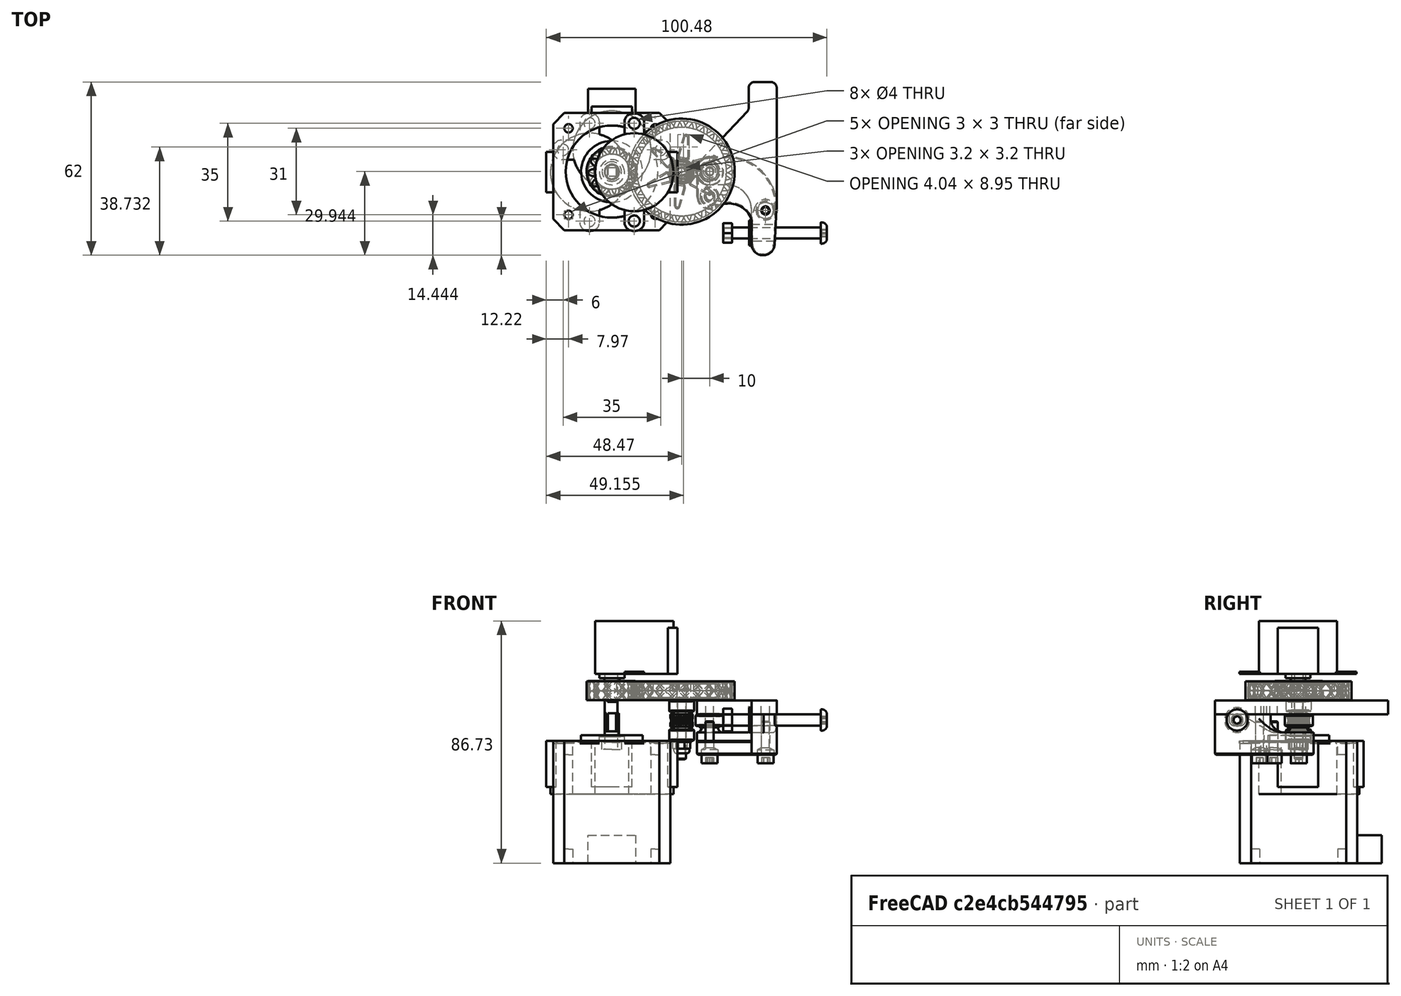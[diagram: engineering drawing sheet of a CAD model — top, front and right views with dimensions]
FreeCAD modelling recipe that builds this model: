
FCSTD DOCUMENT  (FreeCAD 0.16R6703 (Git))
Label: extruder-drive
License: All rights reserved
LicenseURL: http://en.wikipedia.org/wiki/All_rights_reserved
objects: Part::Cylinder×28, Part::Cut×24, Part::Feature×22, Part::MultiFuse×22, Part::Box×21, Part::Fillet×17, Part::Chamfer×5, Part::Mirroring×2, App::DocumentObjectGroup×1
note: 141 computed .brp shape members not serialized (recipe doc carries the construction recipe); baked Part::Feature solids carry a one-line shape summary decoded from their .brp

FEATURE [Part::Feature] Part__Feature  label="408-nema17-stepper"
  Placement = pos=(-0.129787,7.22389,-17.7265) rot=(0,0,-1;1.5708rad)
  shape: bbox 42 x 50.7 x 67.75 mm, 52 faces (baked)
FEATURE [Part::Feature] Part__Feature001  label="279"
  Placement = pos=(33.8857,6.14795,32.8235) rot=(0.910043,0.414513,0;3.14159rad)
  shape: bbox 10 x 10 x 4 mm, 22 faces (baked)
FEATURE [Part::Feature] Part__Feature002  label="1308_lasercut"
  Placement = pos=(34.8702,7.27962,40.5235) rot=(1,0,0;3.14159rad)
  shape: bbox 28.5 x 62 x 5 mm, 26 faces (baked)
FEATURE [Part::Feature] Part__Feature003  label="1309"
  Placement = pos=(34.8702,7.27962,29.0235) rot=(1,0,0;3.14159rad)
  shape: bbox 39.69 x 36.58 x 16.55 mm, 81 faces (baked)
FEATURE [Part::Feature] Part__Feature004  label="1193"
  Placement = pos=(39.681,-14.7761,33.5235) rot=(0.447214,0.774597,0.447214;1.82348rad)
  shape: bbox 3.2 x 7 x 8.083 mm, 26 faces (baked)
FEATURE [Part::Feature] Part__Feature005  label="650"
  Placement = pos=(74.681,-14.7761,33.5235) rot=(-0.322847,0.889685,-0.322847;1.68742rad)
  shape: bbox 37.2 x 8.193 x 8.193 mm, 18 faces (baked)
FEATURE [Part::Feature] Part__Feature006  label="1185"
  Placement = pos=(49.0702,-14.7761,33.5235) rot=(0.682107,-0.263555,0.682107;3.65698rad)
  shape: bbox 0.8 x 9 x 9 mm, 6 faces (baked)
FEATURE [Part::Feature] Part__Feature007  label="212"
  Placement = pos=(34.8702,7.27962,35.8235) rot=(0.929679,0.36837,0;3.14159rad)
  shape: bbox 7 x 7 x 0.5 mm, 6 faces (baked)
FEATURE [Part::Feature] Part__Feature008  label="257"
  Placement = pos=(34.8702,7.27962,21.0235) rot=(0.969952,-0.243295,0;3.14159rad)
  shape: bbox 5.7 x 5.7 x 15 mm, 16 faces (baked)
FEATURE [Part::Feature] Part__Feature010  label="212001"
  Placement = pos=(24.8702,7.22389,26.1235) rot=(0.905883,0.423527,0;3.14159rad)
  shape: bbox 7 x 7 x 0.5 mm, 6 faces (baked)
FEATURE [Part::Feature] Part__Feature011  label="212002"
  Placement = pos=(34.8702,7.27962,31.3235) rot=(0.929679,0.36837,0;3.14159rad)
  shape: bbox 7 x 7 x 0.5 mm, 6 faces (baked)
FEATURE [Part::Feature] Part__Feature012  label="448"
  Placement = pos=(24.8702,7.22389,30.1235) rot=(0,0,1;0rad)
  shape: bbox 8.761 x 8.744 x 6.4 mm, 204 faces (baked)
FEATURE [Part::Feature] Part__Feature013  label="423"
  Placement = pos=(24.8702,7.22389,39.0235) rot=(0,0,1;0.10732rad)
  shape: bbox 9 x 9 x 4 mm, 22 faces (baked)
FEATURE [Part::Feature] Part__Feature014  label="423001"
  Placement = pos=(24.8702,7.22389,28.6235) rot=(0,0,1;3.74342rad)
  shape: bbox 9 x 9 x 4 mm, 22 faces (baked)
FEATURE [Part::Feature] Part__Feature015  label="113"
  Placement = pos=(24.8702,7.22389,44.4235) rot=(0,0,1;3.01463rad)
  shape: bbox 6.3 x 5.858 x 27.5 mm, 19 faces (baked)
FEATURE [Part::Feature] Part__Feature016  label="204"
  Placement = pos=(24.8702,7.22389,25.6235) rot=(0.995731,-0.092303,0;3.14159rad)
  shape: bbox 6.243 x 5.99 x 4 mm, 28 faces (baked)
FEATURE [Part::Feature] Part__Feature017  label="1310_ISO - RH Helical gear 1M 17T 45HA 20PA 12FW ---17A75H50L0.8N"
  Placement = pos=(-0.129787,7.22389,44) rot=(0.464719,0.753705,-0.464719;1.84986rad)
  shape: bbox 18 x 18 x 13.32 mm, 178 faces (baked)
FEATURE [Part::Feature] Part__Feature018  label="1311_ISO - RH Helical gear 1M 17T 45HA 20PA 12FW ---17A75H50L0.8N"
  Placement = pos=(24.8702,7.22389,47.0235) rot=(0.063312,0.995983,-0.063312;1.57482rad)
  shape: bbox 37.39 x 37.38 x 6 mm, 421 faces (baked)
FEATURE [Part::Feature] Part__Feature019  label="1306"
  Placement = pos=(-0.129787,7.22389,26.0235) rot=(0,0,-1;1.5708rad)
  shape: bbox 70.89 x 54.16 x 21.5 mm, 245 faces (baked)
FEATURE [Part::Feature] Part__Feature020  label="257001"
  Placement = pos=(34.8702,-1.72038,21.0235) rot=(0.016076,0.999871,0;3.14159rad)
  shape: bbox 5.7 x 5.7 x 15 mm, 16 faces (baked)
FEATURE [Part::Feature] Part__Feature021  label="257002"
  Placement = pos=(54.8702,-6.72038,21.0235) rot=(0.293708,0.955895,0;3.14159rad)
  shape: bbox 5.7 x 5.7 x 15 mm, 16 faces (baked)
FEATURE [Part::Feature] Part__Feature026  label="212003"
  Placement = pos=(24.8702,7.22389,41.0235) rot=(0.929679,0.36837,0;3.14159rad)
  shape: bbox 7 x 7 x 0.5 mm, 6 faces (baked)
FEATURE [Part::Cylinder] Cylinder
  Angle = 360
  Height = 19
  Radius = 14
FEATURE [Part::Box] Box  label="Cube"
  Height = 16.5
  Length = 10
  Placement = pos=(5.5,-7.25,2.5) rot=(0,0,1;0rad)
  Width = 14.5
FEATURE [Part::Box] Box001  label="Cube001"
  Height = 0.8
  Length = 7
  Placement = pos=(-3.5,-21,18.2) rot=(0,0,1;0rad)
  Width = 42
FEATURE [Part::Cylinder] Cylinder001  label="mounting-hole-1"
  Angle = 360
  Height = 20
  Placement = pos=(0,17.5,14) rot=(0,0,1;0rad)
  Radius = 2
FEATURE [Part::Cylinder] Cylinder002  label="mounting-hole-2"
  Angle = 360
  Height = 20
  Placement = pos=(0,-17.5,14) rot=(0,0,1;0rad)
  Radius = 2
FEATURE [Part::Fillet] Fillet
  Base = -> Box001
  Edges = 1 edges r=3: [Edge5]
FEATURE [Part::Fillet] Fillet001
  Base = -> Fillet
  Edges = 1 edges r=3: [Edge15]
FEATURE [Part::Fillet] Fillet002
  Base = -> Fillet001
  Edges = 1 edges r=3: [Edge14]
FEATURE [Part::Fillet] Fillet003
  Base = -> Fillet002
  Edges = 1 edges r=3: [Edge16]
FEATURE [Part::Cylinder] Cylinder003  label="motor-shaft-cylinder"
  Angle = 360
  Height = 28
  Placement = pos=(-8,0,1) rot=(0,0,1;0rad)
  Radius = 2.5
FEATURE [Part::Cylinder] Cylinder004  label="shaft-boss"
  Angle = 360
  Height = 19.5
  Placement = pos=(-8,0,1) rot=(0,0,1;0rad)
  Radius = 4.5
FEATURE [Part::Box] Box002  label="Cube002"
  Height = 10
  Length = 10
  Placement = pos=(-6.5,-5,22.5) rot=(0,0,1;0rad)
  Width = 10
FEATURE [Part::Box] Box003  label="Cube003"
  Height = 10
  Length = 10
  Placement = pos=(-19.5,-5,22.5) rot=(0,0,1;0rad)
  Width = 10
FEATURE [Part::Cut] Cut
  Base = -> Cylinder003
  Tool = -> Box003
FEATURE [Part::Cut] Cut001  label="motor-shaft"
  Base = -> Cut
  Tool = -> Box002
FEATURE [Part::MultiFuse] Fusion
  Shapes = -> [Cylinder,Box]
FEATURE [Part::MultiFuse] Fusion001
  Shapes = -> [Fusion,Fillet003]
FEATURE [Part::MultiFuse] Fusion002
  Shapes = -> [Fusion001,Cylinder004]
FEATURE [Part::Cut] Cut002
  Base = -> Fusion002
  Tool = -> Cylinder001
FEATURE [Part::Cut] Cut003  label="motor-body"
  Base = -> Cut002
  Tool = -> Cylinder002
FEATURE [Part::MultiFuse] Fusion003  label="28BYJ-48-motor"
  Placement = pos=(7.9,7,7) rot=(0,0,1;0rad)
  Shapes = -> [Cut001,Cut003]
FEATURE [Part::Cylinder] Cylinder005
  Angle = 360
  Height = 19
  Radius = 14
FEATURE [Part::Box] Box004  label="Cube004"
  Height = 16.5
  Length = 10
  Placement = pos=(5.5,-7.25,2.5) rot=(0,0,1;0rad)
  Width = 14.5
FEATURE [Part::Box] Box005  label="Cube005"
  Height = 0.8
  Length = 7
  Placement = pos=(-3.5,-21,18.2) rot=(0,0,1;0rad)
  Width = 42
FEATURE [Part::Cylinder] Cylinder006  label="mounting-hole-003"
  Angle = 360
  Height = 20
  Placement = pos=(0,17.5,14) rot=(0,0,1;0rad)
  Radius = 2
FEATURE [Part::Cylinder] Cylinder007  label="mounting-hole-004"
  Angle = 360
  Height = 20
  Placement = pos=(0,-17.5,14) rot=(0,0,1;0rad)
  Radius = 2
FEATURE [Part::Fillet] Fillet004
  Base = -> Box005
  Edges = 1 edges r=3: [Edge5]
FEATURE [Part::Fillet] Fillet005
  Base = -> Fillet004
  Edges = 1 edges r=3: [Edge15]
FEATURE [Part::Fillet] Fillet006
  Base = -> Fillet005
  Edges = 1 edges r=3: [Edge14]
FEATURE [Part::Fillet] Fillet007
  Base = -> Fillet006
  Edges = 1 edges r=3: [Edge16]
FEATURE [Part::Cylinder] Cylinder008  label="motor-shaft-cylinder001"
  Angle = 360
  Height = 28
  Placement = pos=(-8,0,1) rot=(0,0,1;0rad)
  Radius = 2.5
FEATURE [Part::Cylinder] Cylinder009  label="shaft-boss001"
  Angle = 360
  Height = 19.5
  Placement = pos=(-8,0,1) rot=(0,0,1;0rad)
  Radius = 4.5
FEATURE [Part::Box] Box006  label="Cube006"
  Height = 10
  Length = 10
  Placement = pos=(-6.5,-5,22.5) rot=(0,0,1;0rad)
  Width = 10
FEATURE [Part::Box] Box007  label="Cube007"
  Height = 10
  Length = 10
  Placement = pos=(-19.5,-5,22.5) rot=(0,0,1;0rad)
  Width = 10
FEATURE [Part::Cut] Cut004
  Base = -> Cylinder008
  Tool = -> Box007
FEATURE [Part::Cut] Cut005  label="motor-shaft001"
  Base = -> Cut004
  Tool = -> Box006
FEATURE [Part::MultiFuse] Fusion004
  Shapes = -> [Cylinder005,Box004]
FEATURE [Part::MultiFuse] Fusion005
  Shapes = -> [Fusion004,Fillet007]
FEATURE [Part::MultiFuse] Fusion006
  Shapes = -> [Fusion005,Cylinder009]
FEATURE [Part::Cut] Cut006
  Base = -> Fusion006
  Tool = -> Cylinder006
FEATURE [Part::Cut] Cut007  label="motor-body001"
  Base = -> Cut006
  Tool = -> Cylinder007
FEATURE [Part::MultiFuse] Fusion007  label="28BYJ-48-motor001"
  Placement = pos=(-0.1,15,7) rot=(0,0,1;1.5708rad)
  Shapes = -> [Cut005,Cut007]
FEATURE [Part::Cylinder] Cylinder010
  Angle = 360
  Height = 19
  Radius = 14
FEATURE [Part::Box] Box008  label="Cube008"
  Height = 16.5
  Length = 10
  Placement = pos=(5.5,-7.25,2.5) rot=(0,0,1;0rad)
  Width = 14.5
FEATURE [Part::Box] Box009  label="Cube009"
  Height = 0.8
  Length = 7
  Placement = pos=(-3.5,-21,18.2) rot=(0,0,1;0rad)
  Width = 42
FEATURE [Part::Cylinder] Cylinder011  label="mounting-hole-005"
  Angle = 360
  Height = 20
  Placement = pos=(0,17.5,14) rot=(0,0,1;0rad)
  Radius = 2
FEATURE [Part::Cylinder] Cylinder012  label="mounting-hole-006"
  Angle = 360
  Height = 20
  Placement = pos=(0,-17.5,14) rot=(0,0,1;0rad)
  Radius = 2
FEATURE [Part::Fillet] Fillet008
  Base = -> Box009
  Edges = 1 edges r=3: [Edge5]
FEATURE [Part::Fillet] Fillet009
  Base = -> Fillet008
  Edges = 1 edges r=3: [Edge15]
FEATURE [Part::Fillet] Fillet010
  Base = -> Fillet009
  Edges = 1 edges r=3: [Edge14]
FEATURE [Part::Fillet] Fillet011
  Base = -> Fillet010
  Edges = 1 edges r=3: [Edge16]
FEATURE [Part::Cylinder] Cylinder013  label="motor-shaft-cylinder002"
  Angle = 360
  Height = 28
  Placement = pos=(-8,0,1) rot=(0,0,1;0rad)
  Radius = 2.5
FEATURE [Part::Cylinder] Cylinder014  label="shaft-boss002"
  Angle = 360
  Height = 19.5
  Placement = pos=(-8,0,1) rot=(0,0,1;0rad)
  Radius = 4.5
FEATURE [Part::Box] Box010  label="Cube010"
  Height = 10
  Length = 10
  Placement = pos=(-6.5,-5,22.5) rot=(0,0,1;0rad)
  Width = 10
FEATURE [Part::Box] Box011  label="Cube011"
  Height = 10
  Length = 10
  Placement = pos=(-19.5,-5,22.5) rot=(0,0,1;0rad)
  Width = 10
FEATURE [Part::Cut] Cut008
  Base = -> Cylinder013
  Tool = -> Box011
FEATURE [Part::Cut] Cut009  label="motor-shaft002"
  Base = -> Cut008
  Tool = -> Box010
FEATURE [Part::MultiFuse] Fusion008
  Shapes = -> [Cylinder010,Box008]
FEATURE [Part::MultiFuse] Fusion009
  Shapes = -> [Fusion008,Fillet011]
FEATURE [Part::MultiFuse] Fusion010
  Shapes = -> [Fusion009,Cylinder014]
FEATURE [Part::Cut] Cut010
  Base = -> Fusion010
  Tool = -> Cylinder011
FEATURE [Part::Cut] Cut011  label="motor-body002"
  Base = -> Cut010
  Tool = -> Cylinder012
FEATURE [Part::MultiFuse] Fusion011  label="28BYJ-48-motor002"
  Placement = pos=(-8.1,7,7) rot=(0,0,1;3.14159rad)
  Shapes = -> [Cut009,Cut011]
FEATURE [Part::Cylinder] Cylinder015
  Angle = 360
  Height = 19
  Radius = 14
FEATURE [Part::Box] Box012  label="Cube012"
  Height = 16.5
  Length = 10
  Placement = pos=(5.5,-7.25,2.5) rot=(0,0,1;0rad)
  Width = 14.5
FEATURE [Part::Box] Box013  label="Cube013"
  Height = 0.8
  Length = 7
  Placement = pos=(-3.5,-21,18.2) rot=(0,0,1;0rad)
  Width = 42
FEATURE [Part::Cylinder] Cylinder016  label="mounting-hole-007"
  Angle = 360
  Height = 20
  Placement = pos=(0,17.5,14) rot=(0,0,1;0rad)
  Radius = 2
FEATURE [Part::Cylinder] Cylinder017  label="mounting-hole-008"
  Angle = 360
  Height = 20
  Placement = pos=(0,-17.5,14) rot=(0,0,1;0rad)
  Radius = 2
FEATURE [Part::Fillet] Fillet012
  Base = -> Box013
  Edges = 1 edges r=3: [Edge5]
FEATURE [Part::Fillet] Fillet013
  Base = -> Fillet012
  Edges = 1 edges r=3: [Edge15]
FEATURE [Part::Fillet] Fillet014
  Base = -> Fillet013
  Edges = 1 edges r=3: [Edge14]
FEATURE [Part::Fillet] Fillet015
  Base = -> Fillet014
  Edges = 1 edges r=3: [Edge16]
FEATURE [Part::Cylinder] Cylinder018  label="motor-shaft-cylinder003"
  Angle = 360
  Height = 28
  Placement = pos=(-8,0,1) rot=(0,0,1;0rad)
  Radius = 2.7
FEATURE [Part::Cylinder] Cylinder019  label="shaft-boss003"
  Angle = 360
  Height = 19.5
  Placement = pos=(-8,0,1) rot=(0,0,1;0rad)
  Radius = 4.5
FEATURE [Part::Box] Box014  label="Cube014"
  Height = 10
  Length = 10
  Placement = pos=(-6.4,-5,22.5) rot=(0,0,1;0rad)
  Width = 10
FEATURE [Part::Box] Box015  label="Cube015"
  Height = 10
  Length = 10
  Placement = pos=(-19.6,-5,22.5) rot=(0,0,1;0rad)
  Width = 10
FEATURE [Part::Cut] Cut012
  Base = -> Cylinder018
  Tool = -> Box015
FEATURE [Part::Cut] Cut013  label="motor-shaft003"
  Base = -> Cut012
  Tool = -> Box014
FEATURE [Part::MultiFuse] Fusion012
  Shapes = -> [Cylinder015,Box012]
FEATURE [Part::MultiFuse] Fusion013
  Shapes = -> [Fusion012,Fillet015]
FEATURE [Part::MultiFuse] Fusion014
  Shapes = -> [Fusion013,Cylinder019]
FEATURE [Part::Cut] Cut014
  Base = -> Fusion014
  Tool = -> Cylinder016
FEATURE [Part::Cut] Cut015  label="motor-body003"
  Base = -> Cut014
  Tool = -> Cylinder017
FEATURE [Part::MultiFuse] Fusion015  label="28BYJ-48-motor003"
  Placement = pos=(7.9,7,7) rot=(0,0,1;0rad)
  Shapes = -> [Cut013,Cut015]
FEATURE [Part::Mirroring] Part__Mirroring  label="28BYJ48-motor"
  Base = (0,0,0)
  Normal = (0,0,1)
  Placement = pos=(0,0,76) rot=(0,0,1;0rad)
  Source = -> Fusion015
FEATURE [Part::Box] Box016  label="Cube016"
  Height = 70
  Length = 70
  Placement = pos=(-66,-27,0) rot=(0,0,1;0rad)
  Width = 70
FEATURE [Part::Cut] Cut016
  Base = -> Part__Feature019
  Tool = -> Box016
FEATURE [Part::Box] Box017  label="Cube017"
  Height = 24
  Length = 18
  Placement = pos=(2,-13.8,26) rot=(0,0,1;0rad)
  Width = 42
FEATURE [Part::Box] Box018  label="Cube018"
  Height = 10
  Length = 10
  Placement = pos=(14,-18,40.5) rot=(0,0,1;0rad)
  Width = 10
FEATURE [Part::Box] Box019  label="Cube019"
  Height = 10
  Length = 10
  Placement = pos=(14,20,40.5) rot=(0,0,1;0rad)
  Width = 10
FEATURE [Part::MultiFuse] Fusion016
  Shapes = -> [Box018,Box019]
FEATURE [Part::Cut] Cut017
  Base = -> Cut016
  Tool = -> Fusion016
FEATURE [Part::MultiFuse] Fusion017
  Shapes = -> [Box017,Cut017]
FEATURE [Part::Cylinder] Cylinder020  label="Cylinder016"
  Angle = 360
  Height = 15
  Placement = pos=(25,7.3,40.5) rot=(0,0,1;0rad)
  Radius = 20
FEATURE [Part::Cylinder] Cylinder021  label="Cylinder017"
  Angle = 360
  Height = 22
  Placement = pos=(0,7.3,37.5) rot=(0,0,1;0rad)
  Radius = 10.5
FEATURE [Part::MultiFuse] Fusion018
  Shapes = -> [Cylinder020,Cylinder021]
FEATURE [Part::Cut] Cut018
  Base = -> Fusion017
  Tool = -> Fusion018
FEATURE [Part::Cylinder] Cylinder022  label="Cylinder018"
  Angle = 360
  Height = 10
  Placement = pos=(0,7,30.7) rot=(0,0,1;0rad)
  Radius = 13
FEATURE [Part::Cut] Cut019
  Base = -> Part__Feature017
  Tool = -> Cylinder022
FEATURE [Part::Cylinder] Cylinder023  label="Cylinder019"
  Angle = 360
  Height = 6.7
  Placement = pos=(-0.15,7.2,40.7) rot=(0,0,1;0rad)
  Radius = 6
FEATURE [Part::MultiFuse] Fusion019
  Shapes = -> [Cut019,Cylinder023]
FEATURE [Part::Cut] Cut020  label="motor-shaft004"
  Base = -> Cut012
  Tool = -> Box014
FEATURE [Part::Mirroring] Part__Mirroring001  label="motor-shaft004 (Mirror #2)"
  Base = (0,0,0)
  Normal = (0,0,1)
  Placement = pos=(7.9,7.2,69) rot=(0,0,1;0rad)
  Source = -> Cut020
FEATURE [Part::Cut] Cut021  label="drive-gear"
  Base = -> Fusion019
  Tool = -> Part__Mirroring001
FEATURE [App::DocumentObjectGroup] Group  label="Not-used"
  Group = -> [Fusion003,Fusion007,Fusion011,Part__Feature]
FEATURE [Part::Cylinder] Cylinder024  label="Cylinder020"
  Angle = 360
  Height = 40
  Placement = pos=(5,-10.5,14) rot=(0,0,1;0rad)
  Radius = 2.1
FEATURE [Part::Cylinder] Cylinder025  label="Cylinder021"
  Angle = 360
  Height = 40
  Placement = pos=(10,-10.5,14) rot=(0,0,1;0rad)
  Radius = 2.1
FEATURE [Part::Box] Box020  label="Cube020"
  Height = 44
  Length = 5
  Placement = pos=(5,-12.6,11) rot=(0,0,1;0rad)
  Width = 4.2
FEATURE [Part::MultiFuse] Fusion020  label="m4-slot"
  Placement = pos=(0.5,35,0) rot=(0,0,1;0rad)
  Shapes = -> [Cylinder024,Cylinder025,Box020]
FEATURE [Part::MultiFuse] Fusion021  label="m4-slot001"
  Placement = pos=(0.5,0,0) rot=(0,0,1;0rad)
  Shapes = -> [Cylinder024,Cylinder025,Box020]
FEATURE [Part::Cut] Cut022
  Base = -> Cut018
  Tool = -> Fusion020
FEATURE [Part::Cut] Cut023  label="blank-body"
  Base = -> Cut022
  Tool = -> Fusion021
FEATURE [Part::Chamfer] Chamfer
  Base = -> Cut023
  Edges = 3 edges r=0.5: [Edge7,Edge44,Edge45]
FEATURE [Part::Chamfer] Chamfer001
  Base = -> Chamfer
  Edges = 5 edges r=0.5: [Edge76,Edge77,Edge78,Edge79,Edge80]
FEATURE [Part::Chamfer] Chamfer002
  Base = -> Chamfer001
  Edges = 5 edges r=0.5: [Edge10,Edge11,Edge12,Edge13,Edge14]
FEATURE [Part::Fillet] Fillet016
  Base = -> Chamfer002
  Edges = 1 edges r=2: [Edge205]
FEATURE [Part::Chamfer] Chamfer003
  Base = -> Fillet016
  Edges = 1 edges r=1: [Edge5]
FEATURE [Part::Chamfer] Chamfer004  label="body"
  Base = -> Chamfer003
  Edges = 1 edges r=1: [Edge6]
FEATURE [Part::Cylinder] Cylinder026  label="drive-gear-blank"
  Angle = 360
  Height = 6.7
  Placement = pos=(-0.15,7.2,40.7) rot=(0,0,1;0rad)
  Radius = 9
FEATURE [Part::Cylinder] Cylinder027  label="driven-gear-blank"
  Angle = 360
  Height = 6.7
  Placement = pos=(24.85,7.2,40.7) rot=(0,0,1;0rad)
  Radius = 19
